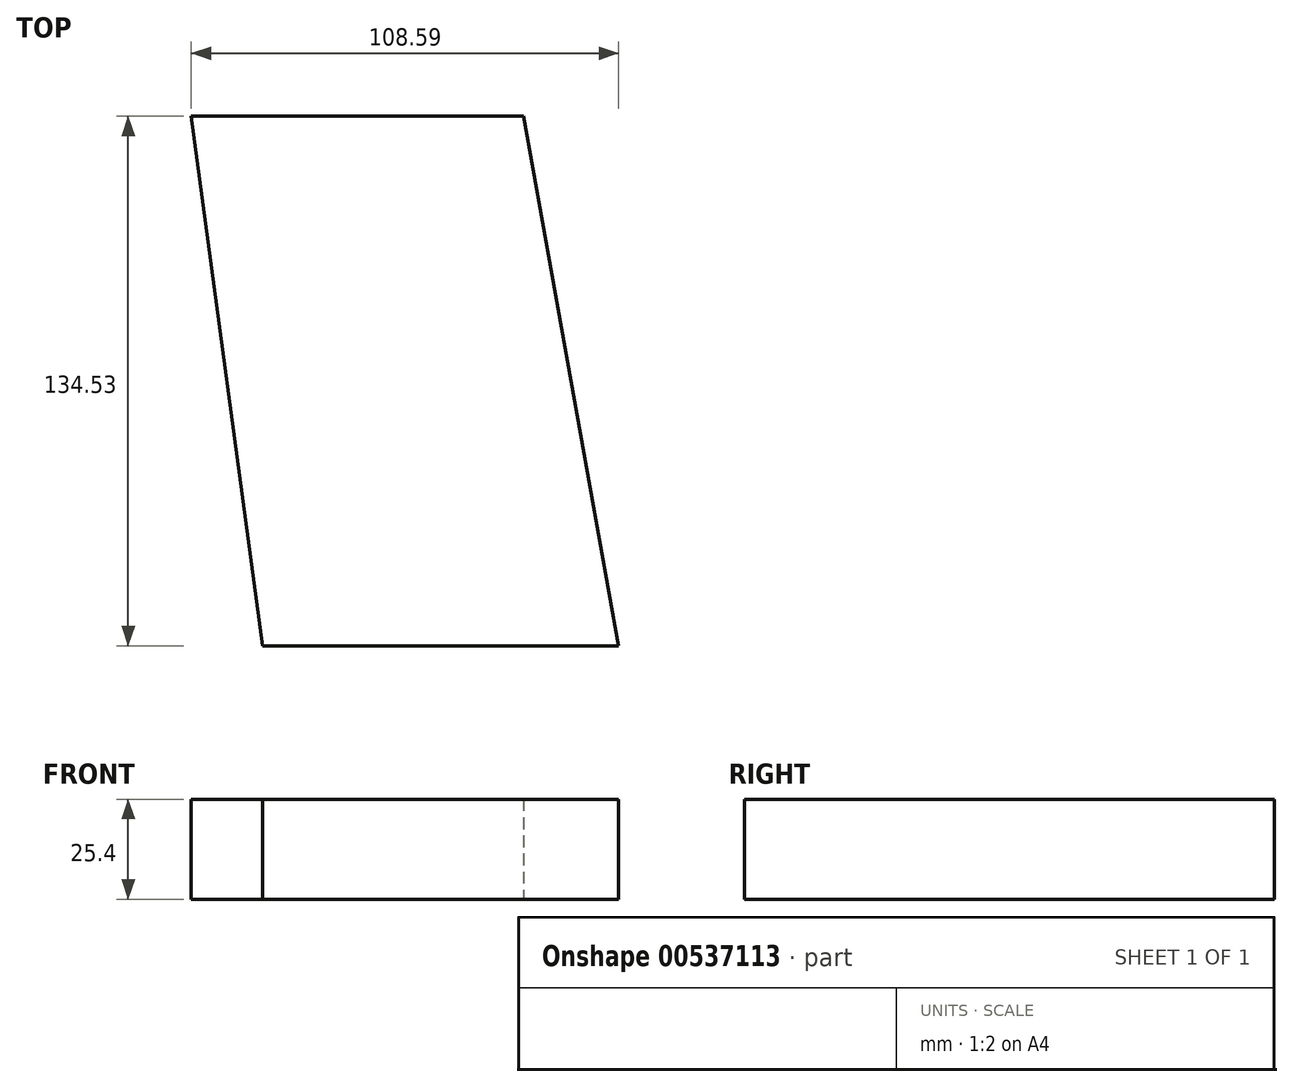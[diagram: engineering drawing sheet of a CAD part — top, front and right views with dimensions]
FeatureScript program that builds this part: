
annotation { "Feature Type Name" : "Feature", "Feature Type Description" : "" }
export const myFeature = defineFeature(function(context is Context, id is Id, definition is map)
    precondition{}
    {
        {
            var Q0;
            Q0=qCreatedBy(makeId("Top.planeOp"),FACE);
            var sketch = newSketch(context, id + "F0", { "sketchPlane" : qUnion([Q0])});
            skLineSegment(sketch, "E0", {"start": v(0, 0) * mm, "end": v(-18.16, 134.53) * mm});
            skLineSegment(sketch, "E1", {"start": v(-18.16, 134.53) * mm, "end": v(66.21, 134.53) * mm});
            skLineSegment(sketch, "E2", {"start": v(66.21, 134.53) * mm, "end": v(90.43, 0) * mm});
            skLineSegment(sketch, "E3", {"start": v(90.43, 0) * mm, "end": v(0, 0) * mm});
            skLineSegment(sketch, "E4", {"start": v(16.24, 199.94) * mm, "end": v(104.41, 199.94) * mm});
            skLineSegment(sketch, "E5", {"start": v(104.41, 199.94) * mm, "end": v(85.66, 200.95) * mm});
            skSolve(sketch);
        }
        {
            var Q0;
            Q0 = qSketchRegion(id + "F0", true);
            extrude(context, id + "F1", {"entities" : qUnion([Q0]), "depth" : 25.4 * mm, "offsetDistance" : 25.4 * mm});
        }
    });
